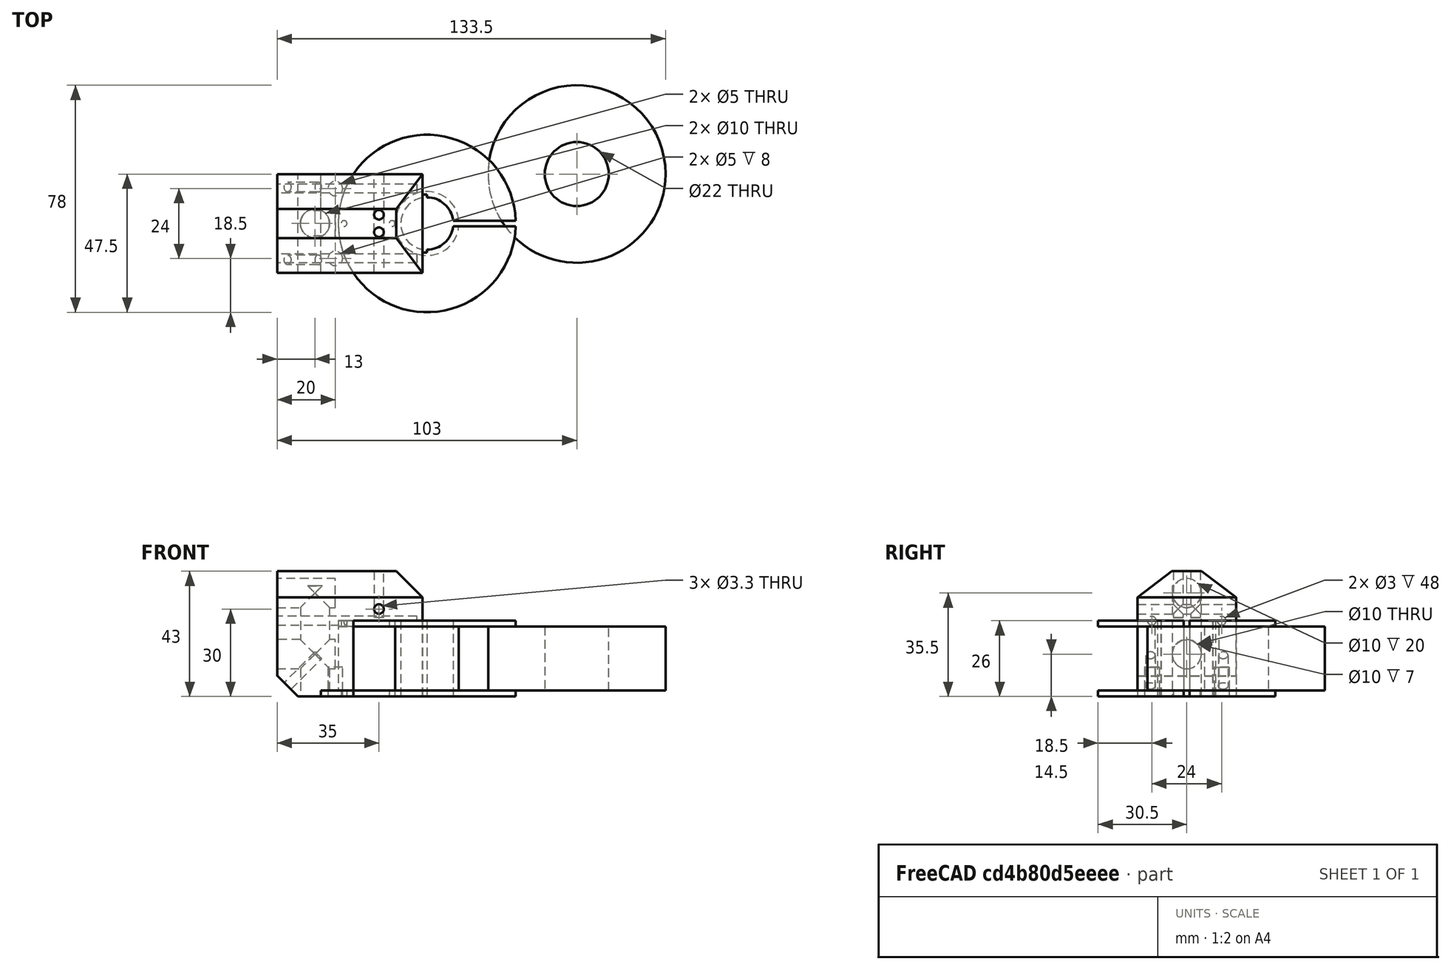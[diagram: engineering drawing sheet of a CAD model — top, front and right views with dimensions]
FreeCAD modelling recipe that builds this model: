
FCSTD DOCUMENT  (FreeCAD 0.20R)
Label: Cryostage
License: All rights reserved
LicenseURL: http://en.wikipedia.org/wiki/All_rights_reserved
objects: Part::Cylinder×24, Part::Cut×18, Part::Box×9, Part::MultiFuse×9, Part::Compound×2
note: 62 computed .brp shape members not serialized (recipe doc carries the construction recipe); baked Part::Feature solids carry a one-line shape summary decoded from their .brp

FEATURE [Part::Box] Box  label="Cube"
  AttacherType = Attacher::AttachEngine3D
  Height = 43
  Length = 50
  Width = 34
FEATURE [Part::Box] Box001  label="Cube001"
  AttacherType = Attacher::AttachEngine3D
  Height = 50
  Length = 100
  Placement = pos=(41,0,43) rot=(0,1,0;0.785398rad)
  Width = 34
FEATURE [Part::Box] Box002  label="Cube002"
  AttacherType = Attacher::AttachEngine3D
  Height = 50
  Length = 72
  Placement = pos=(0,34,34) rot=(1,0,0;0.925025rad)
  Width = 20
FEATURE [Part::Box] Box003  label="Cube003"
  AttacherType = Attacher::AttachEngine3D
  Height = 50
  Length = 72
  Placement = pos=(0,34,34) rot=(1,0,0;0.925025rad)
  Width = 20
FEATURE [Part::Compound] Compound
  Links = -> [Box003]
  Placement = pos=(72,34,0) rot=(0,0,1;3.14159rad)
FEATURE [Part::MultiFuse] Fusion
  Shapes = -> [Box001,Box002,Compound]
FEATURE [Part::Cut] Cut
  Base = -> Box
  Tool = -> Fusion
FEATURE [Part::Cylinder] Cylinder
  Angle = 360
  AttacherType = Attacher::AttachEngine3D
  FirstAngle = 0
  Height = 26
  Radius = 30.5
  SecondAngle = 0
FEATURE [Part::Cylinder] Cylinder001
  Angle = 360
  AttacherType = Attacher::AttachEngine3D
  FirstAngle = 0
  Height = 26
  Radius = 9
  SecondAngle = 0
FEATURE [Part::Cut] Cut001
  Base = -> Cylinder
  Placement = pos=(51.5,17,0) rot=(0,0,1;0rad)
  Tool = -> Cylinder001
FEATURE [Part::Cylinder] Cylinder002
  Angle = 360
  AttacherType = Attacher::AttachEngine3D
  FirstAngle = 0
  Height = 26
  Radius = 30.5
  SecondAngle = 0
FEATURE [Part::Cylinder] Cylinder003
  Angle = 360
  AttacherType = Attacher::AttachEngine3D
  FirstAngle = 0
  Height = 26
  Radius = 9
  SecondAngle = 0
FEATURE [Part::Cut] Cut002  label="CoilHolderBlank"
  Base = -> Cylinder002
  Placement = pos=(51.5,17,0) rot=(0,0,1;0rad)
  Tool = -> Cylinder003
FEATURE [Part::Cut] Cut003
  Base = -> Cut
  Tool = -> Cut001
FEATURE [Part::Cylinder] Cylinder004
  Angle = 360
  AttacherType = Attacher::AttachEngine3D
  FirstAngle = 0
  Height = 22
  Radius = 30.5
  SecondAngle = 0
FEATURE [Part::Cylinder] Cylinder005
  Angle = 360
  AttacherType = Attacher::AttachEngine3D
  FirstAngle = 0
  Height = 22
  Radius = 11
  SecondAngle = 0
FEATURE [Part::Cut] Cut004  label="CoilArea"
  Base = -> Cylinder004
  Placement = pos=(51.5,17,2) rot=(0,0,1;0rad)
  Tool = -> Cylinder005
FEATURE [Part::Cut] Cut005
  Base = -> Cut002
  Tool = -> Cut004
FEATURE [Part::Cylinder] Cylinder006
  Angle = 360
  AttacherType = Attacher::AttachEngine3D
  FirstAngle = 0
  Height = 22
  Radius = 30.5
  SecondAngle = 0
FEATURE [Part::Cylinder] Cylinder007
  Angle = 360
  AttacherType = Attacher::AttachEngine3D
  FirstAngle = 0
  Height = 22
  Radius = 11
  SecondAngle = 0
FEATURE [Part::Cut] Cut006  label="CoilArea001Copper"
  Base = -> Cylinder006
  Placement = pos=(51.5,17,2) rot=(0,0,1;0rad)
  Tool = -> Cylinder007
FEATURE [Part::Box] Box004  label="Cube004"
  AttacherType = Attacher::AttachEngine3D
  Height = 26
  Length = 1.6
  Placement = pos=(49.9,7,0) rot=(0,0,1;0rad)
  Width = 20
FEATURE [Part::Cut] Cut007
  Base = -> Cut005
  Tool = -> Box004
FEATURE [Part::Cylinder] Cylinder008
  Angle = 360
  AttacherType = Attacher::AttachEngine3D
  FirstAngle = 0
  Height = 34
  Placement = pos=(35,34,30) rot=(1,0,0;1.5708rad)
  Radius = 1.65
  SecondAngle = 0
FEATURE [Part::Cylinder] Cylinder009
  Angle = 360
  AttacherType = Attacher::AttachEngine3D
  FirstAngle = 0
  Height = 34
  Placement = pos=(35,20,27) rot=(1,0,0;0rad)
  Radius = 1.65
  SecondAngle = 0
FEATURE [Part::Cylinder] Cylinder010
  Angle = 360
  AttacherType = Attacher::AttachEngine3D
  FirstAngle = 0
  Height = 34
  Placement = pos=(35,14,27) rot=(1,0,0;0rad)
  Radius = 1.65
  SecondAngle = 0
FEATURE [Part::MultiFuse] Fusion001  label="M4Mountscrews01_Corehole"
  Shapes = -> [Cylinder008,Cylinder009,Cylinder010]
FEATURE [Part::Cut] Cut008
  Base = -> Cut003
  Tool = -> Fusion001
FEATURE [Part::Cylinder] Cylinder011
  Angle = 360
  AttacherType = Attacher::AttachEngine3D
  FirstAngle = 0
  Height = 10
  Placement = pos=(20,5,0) rot=(0,0,1;0rad)
  Radius = 2.5
  SecondAngle = 0
FEATURE [Part::Cylinder] Cylinder012
  Angle = 360
  AttacherType = Attacher::AttachEngine3D
  FirstAngle = 0
  Height = 10
  Placement = pos=(20,29,0) rot=(0,0,1;0rad)
  Radius = 2.5
  SecondAngle = 0
FEATURE [Part::MultiFuse] Fusion002  label="BoreholeM6Screws01"
  Shapes = -> [Cylinder012,Cylinder011]
FEATURE [Part::Cut] Cut009
  Base = -> Cut008
  Tool = -> Fusion002
FEATURE [Part::Box] Box005  label="Cube005"
  AttacherType = Attacher::AttachEngine3D
  Height = 2
  Length = 15
  Placement = pos=(15,0,0) rot=(0,0,1;0rad)
  Width = 34
FEATURE [Part::Cylinder] Cylinder013
  Angle = 360
  AttacherType = Attacher::AttachEngine3D
  FirstAngle = 0
  Height = 10
  Placement = pos=(20,5,0) rot=(0,0,1;0rad)
  Radius = 2.5
  SecondAngle = 0
FEATURE [Part::Cylinder] Cylinder014
  Angle = 360
  AttacherType = Attacher::AttachEngine3D
  FirstAngle = 0
  Height = 10
  Placement = pos=(20,29,0) rot=(0,0,1;0rad)
  Radius = 2.5
  SecondAngle = 0
FEATURE [Part::MultiFuse] Fusion003  label="BoreholeM6Screws002"
  Shapes = -> [Cylinder014,Cylinder013]
FEATURE [Part::Cut] Cut010
  Base = -> Box005
  Tool = -> Fusion003
FEATURE [Part::MultiFuse] Fusion004
  Shapes = -> [Cut007,Cut010]
FEATURE [Part::Box] Box006  label="Cube006"
  AttacherType = Attacher::AttachEngine3D
  Height = 2
  Length = 15
  Placement = pos=(15,0,0) rot=(0,0,1;0rad)
  Width = 34
FEATURE [Part::Cut] Cut011
  Base = -> Cut009
  Tool = -> Box006
FEATURE [Part::Box] Box007  label="Cube007"
  AttacherType = Attacher::AttachEngine3D
  Height = 26
  Length = 30
  Placement = pos=(53,16,0) rot=(0,0,1;0rad)
  Width = 2
FEATURE [Part::Cut] Cut012
  Base = -> Fusion004
  Tool = -> Box007
FEATURE [Part::Cylinder] Cylinder015
  Angle = 360
  AttacherType = Attacher::AttachEngine3D
  FirstAngle = 0
  Height = 26
  Placement = pos=(39.5,17,0) rot=(0,0,1;0rad)
  Radius = 1
  SecondAngle = 0
FEATURE [Part::Cylinder] Cylinder016
  Angle = 360
  AttacherType = Attacher::AttachEngine3D
  FirstAngle = 0
  Height = 26
  Placement = pos=(23,17,0) rot=(0,0,1;0rad)
  Radius = 1
  SecondAngle = 0
FEATURE [Part::MultiFuse] Fusion005  label="WireHoles"
  Shapes = -> [Cylinder016,Cylinder015]
FEATURE [Part::Cut] Cut013  label="Coilholder"
  Base = -> Cut012
  Tool = -> Fusion005
FEATURE [Part::Cylinder] Cylinder017  label="NitrogenChamber01"
  Angle = 360
  AttacherType = Attacher::AttachEngine3D
  FirstAngle = 0
  Height = 38
  Placement = pos=(13,17,0) rot=(0,0,1;1.5708rad)
  Radius = 5
  SecondAngle = 0
FEATURE [Part::Cylinder] Cylinder018  label="NitrogenChamber002"
  Angle = 360
  AttacherType = Attacher::AttachEngine3D
  FirstAngle = 0
  Height = 20
  Placement = pos=(0,17,14.5) rot=(0,1,0;1.5708rad)
  Radius = 5
  SecondAngle = 0
FEATURE [Part::Cylinder] Cylinder019  label="NitrogenChamber003"
  Angle = 360
  AttacherType = Attacher::AttachEngine3D
  FirstAngle = 0
  Height = 20
  Placement = pos=(0,17,35.5) rot=(0,1,0;1.5708rad)
  Radius = 5
  SecondAngle = 0
FEATURE [Part::MultiFuse] Fusion006  label="NitrogenChamber"
  Shapes = -> [Cylinder017,Cylinder018,Cylinder019]
FEATURE [Part::Cut] Cut014
  Base = -> Cut011
  Tool = -> Fusion006
FEATURE [Part::Box] Box008  label="Cube008"
  AttacherType = Attacher::AttachEngine3D
  Height = 10
  Length = 10
  Placement = pos=(-7,0,0) rot=(0,1,0;0.785398rad)
  Width = 34
FEATURE [Part::Cut] Cut015
  Base = -> Cut014
  Tool = -> Box008
FEATURE [Part::Cylinder] Cylinder020
  Angle = 360
  AttacherType = Attacher::AttachEngine3D
  FirstAngle = 0
  Height = 20
  Placement = pos=(0,4.5,0) rot=(0,1,0;0.785398rad)
  Radius = 1.65
  SecondAngle = 0
FEATURE [Part::Cylinder] Cylinder021
  Angle = 360
  AttacherType = Attacher::AttachEngine3D
  FirstAngle = 0
  Height = 20
  Placement = pos=(0,29.5,0) rot=(0,1,0;0.785398rad)
  Radius = 1.65
  SecondAngle = 0
FEATURE [Part::MultiFuse] Fusion007  label="M4Screws"
  Shapes = -> [Cylinder020,Cylinder021]
FEATURE [Part::Cut] Cut016
  Base = -> Cut015
  Tool = -> Fusion007
FEATURE [Part::Cylinder] Cylinder022
  Angle = 360
  AttacherType = Attacher::AttachEngine3D
  FirstAngle = 0
  Height = 48
  Placement = pos=(0,5,26) rot=(0,1,0;1.5708rad)
  Radius = 1.5
  SecondAngle = 0
FEATURE [Part::Cylinder] Cylinder023
  Angle = 360
  AttacherType = Attacher::AttachEngine3D
  FirstAngle = 0
  Height = 48
  Placement = pos=(0,29,26) rot=(0,1,0;1.5708rad)
  Radius = 1.5
  SecondAngle = 0
FEATURE [Part::MultiFuse] Fusion008  label="CableDrillHole"
  Shapes = -> [Cylinder022,Cylinder023]
FEATURE [Part::Cut] Cut017  label="Cryostage"
  Base = -> Cut016
  Tool = -> Fusion008
FEATURE [Part::Compound] Compound001  label="StageAssembly"
  Links = -> [Cut013,Cut017]
  Placement = pos=(-51.5,-17,0) rot=(0,0,1;0rad)
